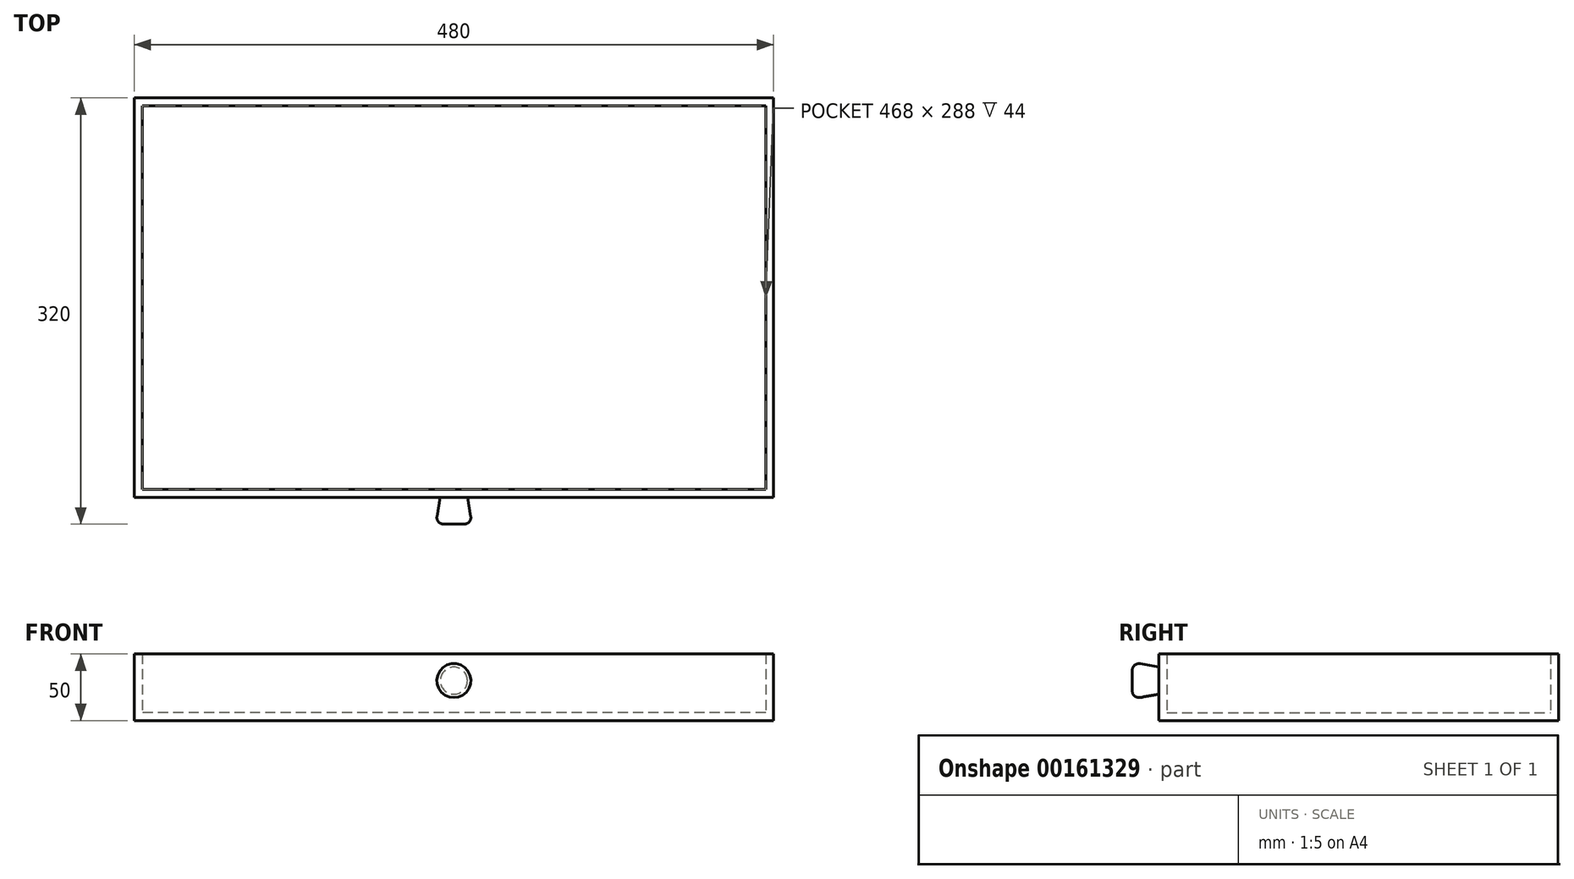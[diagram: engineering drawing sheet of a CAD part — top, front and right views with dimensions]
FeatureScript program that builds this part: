
annotation { "Feature Type Name" : "Feature", "Feature Type Description" : "" }
export const myFeature = defineFeature(function(context is Context, id is Id, definition is map)
    precondition{}
    {
        {
            var Q0;
            Q0=qCreatedBy(makeId("Top.planeOp"),FACE);
            var sketch = newSketch(context, id + "F0", { "sketchPlane" : qUnion([Q0])});
            skLineSegment(sketch, "E0.bottom", {"start": v(349.05, -101.92) * mm, "end": v(-130.95, -101.92) * mm});
            skLineSegment(sketch, "E0.top", {"start": v(349.05, 198.08) * mm, "end": v(-130.95, 198.08) * mm});
            skLineSegment(sketch, "E0.left", {"start": v(349.05, -101.92) * mm, "end": v(349.05, 198.08) * mm});
            skLineSegment(sketch, "E0.right", {"start": v(-130.95, -101.92) * mm, "end": v(-130.95, 198.08) * mm});
            skSolve(sketch);
        }
        {
            var Q0;
            Q0=makeQuery(id+"F0.imprint","IMPRINT",FACE,{"disambiguationData":[TD([[makeQuery(id+"F0.imprint","IMPRINT",EDGE,{"derivedFrom":sQuery(id+"F0.wireOp",EDGE,"E0.bottom")}),-1.0]])]});
            extrude(context, id + "F1", {"entities" : qUnion([Q0]), "depth" : 50 * mm});
        }
        {
            var Q0;
            Q0=makeQuery(id+"F1.opExtrude","CAP_FACE",FACE,{"disambiguationData":[OSD([sQuery(id+"F0.wireOp",EDGE,"E0.bottom"),sQuery(id+"F0.wireOp",EDGE,"E0.top"),sQuery(id+"F0.wireOp",EDGE,"E0.left"),sQuery(id+"F0.wireOp",EDGE,"E0.right")])],"isStart":false});
            shell(context, id + "F2", {"entities" : qUnion([Q0]), "thickness" : 6 * mm});
        }
        {
            var Q0;
            Q0=makeQuery(id+"F1.opExtrude","SWEPT_FACE",FACE,{"disambiguationData":[OSD([sQuery(id+"F0.wireOp",EDGE,"E0.bottom")])]});
            var sketch = newSketch(context, id + "F3", { "sketchPlane" : qUnion([Q0])});
            skCircle(sketch, "E1", {"center": v(109.05, 30) * mm, "radius": 10.19 * mm});
            skSolve(sketch);
        }
        {
            var Q0;
            Q0=makeQuery(id+"F3.imprint","IMPRINT",FACE,{"disambiguationData":[TD([[makeQuery(id+"F3.imprint","IMPRINT",EDGE,{"derivedFrom":sQuery(id+"F3.wireOp",EDGE,"E1")}),1.0]])]});
            extrude(context, id + "F4", {"entities" : qUnion([Q0]), "operationType" : NewBodyOperationType.ADD, "depth" : 20 * mm, "hasDraft" : true, "draftAngle" : 10 * degree});
        }
        {
            var Q0;
            Q0=makeQuery(id+"F4.opExtrude","CAP_EDGE",EDGE,{"disambiguationData":[OSD([sQuery(id+"F3.wireOp",EDGE,"E1")])],"isStart":false});
            fillet(context, id + "F5", {"entities" : qUnion([Q0]), "radius" : 5 * mm, "tangentPropagation" : true, "allowEdgeOverflow" : false});
        }
    });
